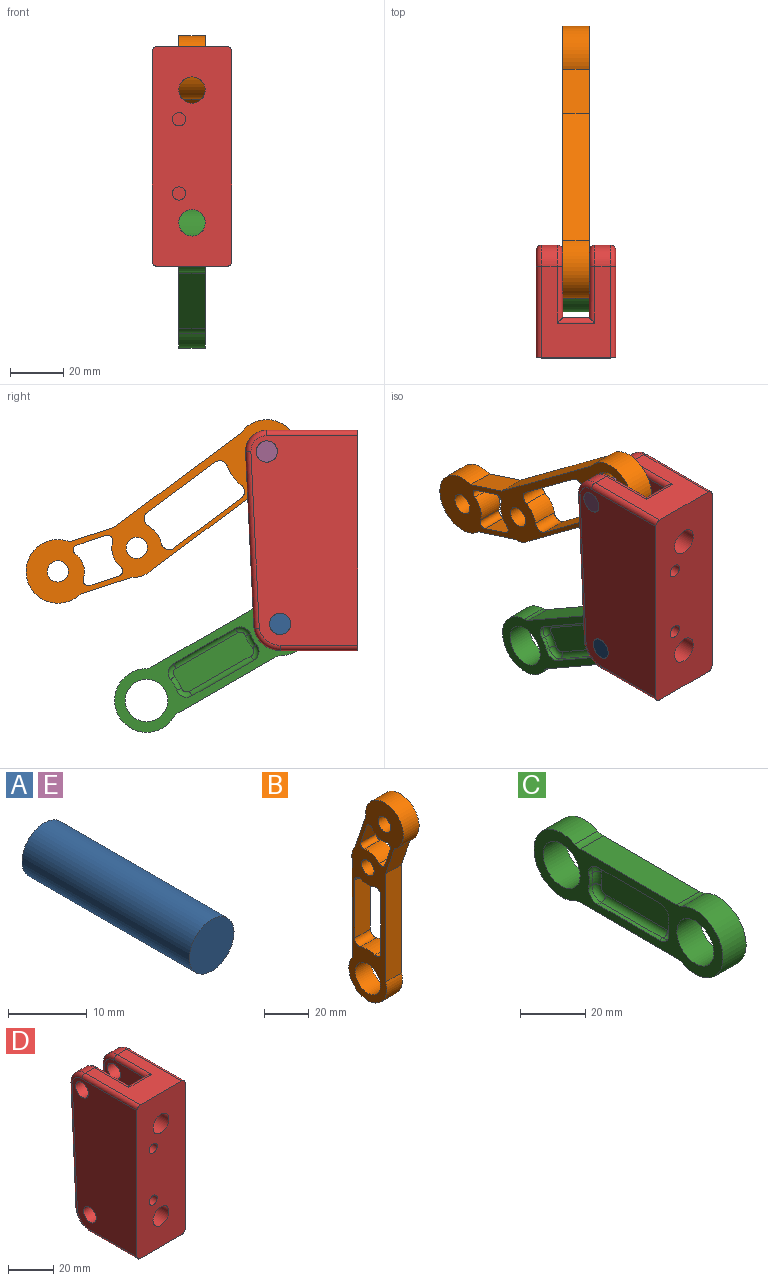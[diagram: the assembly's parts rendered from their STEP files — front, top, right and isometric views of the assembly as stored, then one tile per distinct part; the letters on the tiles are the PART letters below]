
ASSEMBLY  parts=5 mates=4
PART A: 3 faces, bbox 8x30x8 mm
  f0: cylinder r=4mm len=30mm, axis (0,1,0), area 754mm2, adj f1,f2
  f1: plane 8x8mm, normal (0,-1,0), area 50.3mm2, adj f0
  f2: plane 8x8mm, normal (0,1,0), area 50.3mm2, adj f0
PART B: 28 faces, bbox 10x34.6x114.1 mm
  f0: cylinder r=2mm len=10mm, axis (-1,0,0), area 44.3mm2, adj f1,f18,f22,f23
  f1: cylinder r=8mm len=10mm, axis (-1,0,0), area 103mm2, adj f0,f2,f22,f23
  f2: cylinder r=2mm len=10mm, axis (-1,0,0), area 44.3mm2, adj f1,f3,f22,f23
  f3: plane 10.85x10mm, normal (0,-0.95,-0.32), area 114.5mm2, adj f2,f4,f22,f23
  f4: cylinder r=2mm len=10mm, axis (-1,0,0), area 42.5mm2, adj f3,f5,f22,f23
  f5: cylinder r=9.39mm len=10mm, axis (-1,0,0), area 104.2mm2, adj f4,f6,f22,f23
  f6: cylinder r=2mm len=10mm, axis (-1,0,0), area 42.5mm2, adj f5,f18,f22,f23
  f7: cylinder r=15.89mm len=10mm, axis (-1,0,0), area 91.6mm2, adj f22,f23,f24,f27
  f8: plane 31.73x10mm, normal (0,1,0), area 317.3mm2, adj f22,f23,f24,f25
  f9: cylinder r=9.39mm len=10mm, axis (-1,0,0), area 84.2mm2, adj f22,f23,f25,f26
  f10: plane 16.53x10mm, normal (0,-0.95,-0.32), area 174.5mm2, adj f11,f20,f22,f23
  f11: plane 59.57x10mm, normal (0,-1,0), area 595.7mm2, adj f10,f12,f22,f23
  f12: cylinder r=12mm len=24mm, axis (-1,0,0), area 486.4mm2, adj f11,f13,f22,f23
  f13: plane 54.37x10mm, normal (0,1,0), area 543.7mm2, adj f12,f14,f22,f23
  f14: cylinder r=10mm len=10mm, axis (-1,0,0), area 86.2mm2, adj f13,f15,f22,f23
  f15: plane 19.41x10mm, normal (0,0.95,0.32), area 204.8mm2, adj f14,f20,f22,f23
  f16: cylinder r=4mm len=10mm, axis (-1,0,0), area 251.3mm2, adj f22,f23
  f17: cylinder r=4mm len=10mm, axis (-1,0,0), area 251.3mm2, adj f22,f23
  f18: plane 10.85x10mm, normal (0,0.95,0.32), area 114.5mm2, adj f0,f6,f22,f23
  f19: plane 31.73x10mm, normal (0,-1,0), area 317.3mm2, adj f22,f23,f26,f27
  f20: cylinder r=12mm len=24mm, axis (-1,0,0), area 515.2mm2, adj f10,f15,f22,f23
  f21: cylinder r=8mm len=16mm, axis (-1,0,0), area 502.7mm2, adj f22,f23
  f22: plane 114.13x34.6mm, normal (1,0,0), area 1280.1mm2, adj f0,f1,f2,f3,f4,f5,f6,f7
  f23: plane 114.13x34.6mm, normal (-1,0,0), area 1280.1mm2, adj f0,f1,f2,f3,f4,f5,f6,f7
  f24: cylinder r=3mm len=10mm, axis (-1,0,0), area 55.8mm2, adj f7,f8,f22,f23
  f25: cylinder r=3mm len=10mm, axis (-1,0,0), area 60.6mm2, adj f8,f9,f22,f23
  f26: cylinder r=3mm len=10mm, axis (-1,0,0), area 60.6mm2, adj f9,f19,f22,f23
  f27: cylinder r=3mm len=10mm, axis (-1,0,0), area 55.8mm2, adj f7,f19,f22,f23
PART C: 46 faces, bbox 10x82x24 mm
  f0: plane 26.82x2.5mm, normal (0,0,-1), area 67mm2, adj f14,f20,f23,f37
  f1: plane 26.82x2.5mm, normal (0,0,1), area 67mm2, adj f14,f21,f22,f30
  f2: cylinder r=11.75mm len=4.48mm, axis (1,0,0), area 11.3mm2, adj f14,f20,f21,f33
  f3: cylinder r=12mm len=4.5mm, axis (1,0,0), area 11.3mm2, adj f14,f22,f23,f34
  f4: cylinder r=4mm len=4.76mm, axis (1,0,0), area 10.6mm2, adj f15,f16,f17,f39
  f5: cylinder r=4mm len=4.76mm, axis (1,0,0), area 10.6mm2, adj f15,f17,f18,f43
  f6: cylinder r=4mm len=4.75mm, axis (1,0,0), area 10.6mm2, adj f15,f18,f19,f44
  f7: cylinder r=4mm len=4.75mm, axis (1,0,0), area 10.6mm2, adj f15,f16,f19,f40
  f8: plane 42x10mm, normal (0,0,1), area 420mm2, adj f14,f15,f24,f27
  f9: cylinder r=12mm len=24mm, axis (-1,0,0), area 494.6mm2, adj f14,f15,f24,f25
  f10: plane 42x10mm, normal (0,0,-1), area 420mm2, adj f14,f15,f25,f26
  f11: cylinder r=8mm len=16mm, axis (-1,0,0), area 502.7mm2, adj f14,f15
  f12: cylinder r=12mm len=24mm, axis (-1,0,0), area 494.6mm2, adj f14,f15,f26,f27
  f13: cylinder r=8mm len=16mm, axis (-1,0,0), area 502.7mm2, adj f14,f15
  f14: plane 82x24mm, normal (1,0,0), area 775.1mm2, adj f0,f1,f2,f3,f8,f9,f10,f11
  f15: plane 82x24mm, normal (-1,0,0), area 775.1mm2, adj f4,f5,f6,f7,f8,f9,f10,f11
  f16: plane 26.82x1.5mm, normal (0,0,-1), area 40.2mm2, adj f4,f7,f15,f38
  f17: cylinder r=11.75mm len=4.48mm, axis (1,0,0), area 6.8mm2, adj f4,f5,f15,f41
  f18: plane 26.82x1.5mm, normal (0,0,1), area 40.2mm2, adj f5,f6,f15,f45
  f19: cylinder r=12mm len=4.5mm, axis (1,0,0), area 6.8mm2, adj f6,f7,f15,f42
  f20: cylinder r=4mm len=4.76mm, axis (1,0,0), area 17.6mm2, adj f0,f2,f14,f35
  f21: cylinder r=4mm len=4.76mm, axis (1,0,0), area 17.6mm2, adj f1,f2,f14,f31
  f22: cylinder r=4mm len=4.75mm, axis (1,0,0), area 17.6mm2, adj f1,f3,f14,f32
  f23: cylinder r=4mm len=4.75mm, axis (1,0,0), area 17.6mm2, adj f0,f3,f14,f36
  f24: cylinder r=5mm len=10mm, axis (-1,0,0), area 24.5mm2, adj f8,f9,f14,f15
  f25: cylinder r=5mm len=10mm, axis (-1,0,0), area 24.5mm2, adj f9,f10,f14,f15
  f26: cylinder r=5mm len=10mm, axis (-1,0,0), area 24.5mm2, adj f10,f12,f14,f15
  f27: cylinder r=5mm len=10mm, axis (-1,0,0), area 24.5mm2, adj f8,f12,f14,f15
  f28: plane 30.82x10mm, normal (1,0,0), area 302.6mm2, adj f30,f31,f32,f33,f34,f35,f36,f37
  f29: plane 30.82x10mm, normal (-1,0,0), area 302.6mm2, adj f38,f39,f40,f41,f42,f43,f44,f45
  f30: cylinder r=2mm len=26.82mm, axis (0,1,0), area 84.3mm2, adj f1,f28,f31,f32
  f31: torus R=2mm, axis (1,0,0), area 18.1mm2, adj f21,f28,f30,f33
  f32: torus R=2mm, axis (1,0,0), area 18.1mm2, adj f22,f28,f30,f34
  f33: torus R=13.75mm, axis (1,0,0), area 15mm2, adj f2,f28,f31,f35
  f34: torus R=14mm, axis (1,0,0), area 15.1mm2, adj f3,f28,f32,f36
  f35: torus R=2mm, axis (1,0,0), area 18.1mm2, adj f20,f28,f33,f37
  f36: torus R=2mm, axis (1,0,0), area 18.1mm2, adj f23,f28,f34,f37
  f37: cylinder r=2mm len=26.82mm, axis (0,-1,0), area 84.3mm2, adj f0,f28,f35,f36
  f38: cylinder r=2mm len=26.82mm, axis (0,1,0), area 84.3mm2, adj f16,f29,f39,f40
  f39: torus R=2mm, axis (1,0,0), area 18.1mm2, adj f4,f29,f38,f41
  f40: torus R=2mm, axis (1,0,0), area 18.1mm2, adj f7,f29,f38,f42
  f41: torus R=13.75mm, axis (1,0,0), area 15mm2, adj f17,f29,f39,f43
  f42: torus R=14mm, axis (1,0,0), area 15.1mm2, adj f19,f29,f40,f44
  f43: torus R=2mm, axis (1,0,0), area 18.1mm2, adj f5,f29,f41,f45
  f44: torus R=2mm, axis (1,0,0), area 18.1mm2, adj f6,f29,f42,f45
  f45: cylinder r=2mm len=26.82mm, axis (0,-1,0), area 84.3mm2, adj f18,f29,f43,f44
PART D: 48 faces, bbox 30x43x84.5 mm
  f0: plane 83x30mm, normal (0,-1,0), area 2290.2mm2, adj f3,f5,f6,f13,f17,f25,f32,f36
  f1: plane 14.5x10mm, normal (0,1,0), area 105.7mm2, adj f12,f18,f31,f43
  f2: plane 50x10mm, normal (0,1,0), area 421.5mm2, adj f12,f31,f42,f43
  f3: plane 29.34x26mm, normal (0,0,-1), area 534.1mm2, adj f0,f7,f13,f18,f19,f26,f32,f37
  f4: plane 14.5x10mm, normal (0,1,0), area 105.7mm2, adj f12,f20,f31,f42
  f5: plane 34.34x26mm, normal (0,0,1), area 594.1mm2, adj f0,f9,f17,f20,f22,f28,f36,f39
  f6: plane 79x40.34mm, normal (1,0,0), area 2940.1mm2, adj f0,f10,f11,f13,f14,f15,f16,f17
  f7: cylinder r=10mm len=9.82mm, axis (1,0,0), area 82.9mm2, adj f3,f8,f14,f21
  f8: plane 66.88x6mm, normal (0,1,-0.05), area 401.7mm2, adj f7,f9,f15,f23
  f9: cylinder r=8mm len=8mm, axis (1,0,0), area 75.4mm2, adj f5,f8,f16,f24
  f10: cylinder r=4mm len=10mm, axis (1,0,0), area 251.3mm2, adj f6,f12
  f11: cylinder r=4mm len=10mm, axis (1,0,0), area 251.3mm2, adj f6,f12
  f12: plane 79x25.34mm, normal (-1,0,0), area 1755.1mm2, adj f1,f2,f4,f10,f11,f19,f21,f22
  f13: cylinder r=2mm len=29.34mm, axis (0,1,0), area 92.2mm2, adj f0,f3,f6,f14
  f14: torus R=8mm, axis (1,0,0), area 40.1mm2, adj f6,f7,f13,f15
  f15: cylinder r=2mm len=66.97mm, axis (0,0.05,1), area 210.1mm2, adj f6,f8,f14,f16
  f16: torus R=6mm, axis (1,0,0), area 35.8mm2, adj f6,f9,f15,f17
  f17: cylinder r=2mm len=34.34mm, axis (0,-1,0), area 107.9mm2, adj f0,f5,f6,f16
  f18: cylinder r=2mm len=14mm, axis (-1,0,0), area 36mm2, adj f1,f3,f19,f37
  f19: cylinder r=2mm len=16.34mm, axis (0,1,0), area 47.3mm2, adj f3,f12,f18,f21
  f20: cylinder r=2mm len=14mm, axis (1,0,0), area 36mm2, adj f4,f5,f22,f39
  f21: torus R=8mm, axis (1,0,0), area 40.1mm2, adj f7,f12,f19,f23
  f22: cylinder r=2mm len=21.34mm, axis (0,-1,0), area 63mm2, adj f5,f12,f20,f24
  f23: cylinder r=2mm len=66.97mm, axis (0,-0.05,-1), area 210.1mm2, adj f8,f12,f21,f24
  f24: torus R=6mm, axis (1,0,0), area 35.8mm2, adj f9,f12,f22,f23
  f25: plane 79x40.34mm, normal (-1,0,0), area 2940.1mm2, adj f0,f29,f30,f32,f33,f34,f35,f36
  f26: cylinder r=10mm len=9.82mm, axis (-1,0,0), area 82.9mm2, adj f3,f27,f33,f38
  f27: plane 66.88x6mm, normal (0,1,-0.05), area 401.7mm2, adj f26,f28,f34,f40
  f28: cylinder r=8mm len=8mm, axis (-1,0,0), area 75.4mm2, adj f5,f27,f35,f41
  f29: cylinder r=4mm len=10mm, axis (-1,0,0), area 251.3mm2, adj f25,f31
  f30: cylinder r=4mm len=10mm, axis (-1,0,0), area 251.3mm2, adj f25,f31
  f31: plane 79x25.34mm, normal (1,0,0), area 1755.1mm2, adj f1,f2,f4,f29,f30,f37,f38,f39
  f32: cylinder r=2mm len=29.34mm, axis (0,1,0), area 92.2mm2, adj f0,f3,f25,f33
  f33: torus R=8mm, axis (-1,0,0), area 40.1mm2, adj f25,f26,f32,f34
  f34: cylinder r=2mm len=66.97mm, axis (0,0.05,1), area 210.1mm2, adj f25,f27,f33,f35
  f35: torus R=6mm, axis (-1,0,0), area 35.8mm2, adj f25,f28,f34,f36
  f36: cylinder r=2mm len=34.34mm, axis (0,-1,0), area 107.9mm2, adj f0,f5,f25,f35
  f37: cylinder r=2mm len=16.34mm, axis (0,1,0), area 47.3mm2, adj f3,f18,f31,f38
  f38: torus R=8mm, axis (-1,0,0), area 40.1mm2, adj f26,f31,f37,f40
  f39: cylinder r=2mm len=21.34mm, axis (0,-1,0), area 63mm2, adj f5,f20,f31,f41
  f40: cylinder r=2mm len=66.97mm, axis (0,-0.05,-1), area 210.1mm2, adj f27,f31,f38,f41
  f41: torus R=6mm, axis (-1,0,0), area 35.8mm2, adj f28,f31,f39,f40
  f42: cylinder r=5mm len=15mm, axis (0,-1,0), area 471.2mm2, adj f0,f2,f4
  f43: cylinder r=5mm len=15mm, axis (0,-1,0), area 471.2mm2, adj f0,f1,f2
  f44: cylinder r=2.5mm len=6mm, axis (0,-1,0), area 94.2mm2, adj f0,f45
  f45: plane 5x5mm, normal (0,-1,0), area 19.6mm2, adj f44
  f46: cylinder r=2.5mm len=6mm, axis (0,-1,0), area 94.2mm2, adj f0,f47
  f47: plane 5x5mm, normal (0,-1,0), area 19.6mm2, adj f46
PART E: same geometry as A
PLACE A rot(axis=(0.58,-0.58,0.58),120deg) t=(-69.71,-3.49,12.83)mm
PLACE B rot(axis=(-1,0,0),126.6deg) t=(-59.71,50.5,18.63)mm
PLACE C rot(axis=(-1,0,0),29.8deg) t=(-59.71,46.84,-38.85)mm
PLACE D t=(-39.71,-3.49,-10.03)mm fixed
PLACE E rot(axis=(0.58,-0.58,0.58),120deg) t=(-69.71,1.51,77.83)mm
MATE revolute A.f0 <-> C.f11  axis (-1,0,0) through (-54.71,-3.49,-10.03)mm
MATE fastened A.f0 <-> D.f11  axis (-1,0,0) through (-69.71,-3.49,-10.03)mm
MATE fastened E.f0 <-> D.f9  axis (-1,0,0) through (-69.71,1.51,54.97)mm
MATE revolute E.f0 <-> B.f12  axis (-1,0,0) through (-54.71,1.51,54.97)mm
